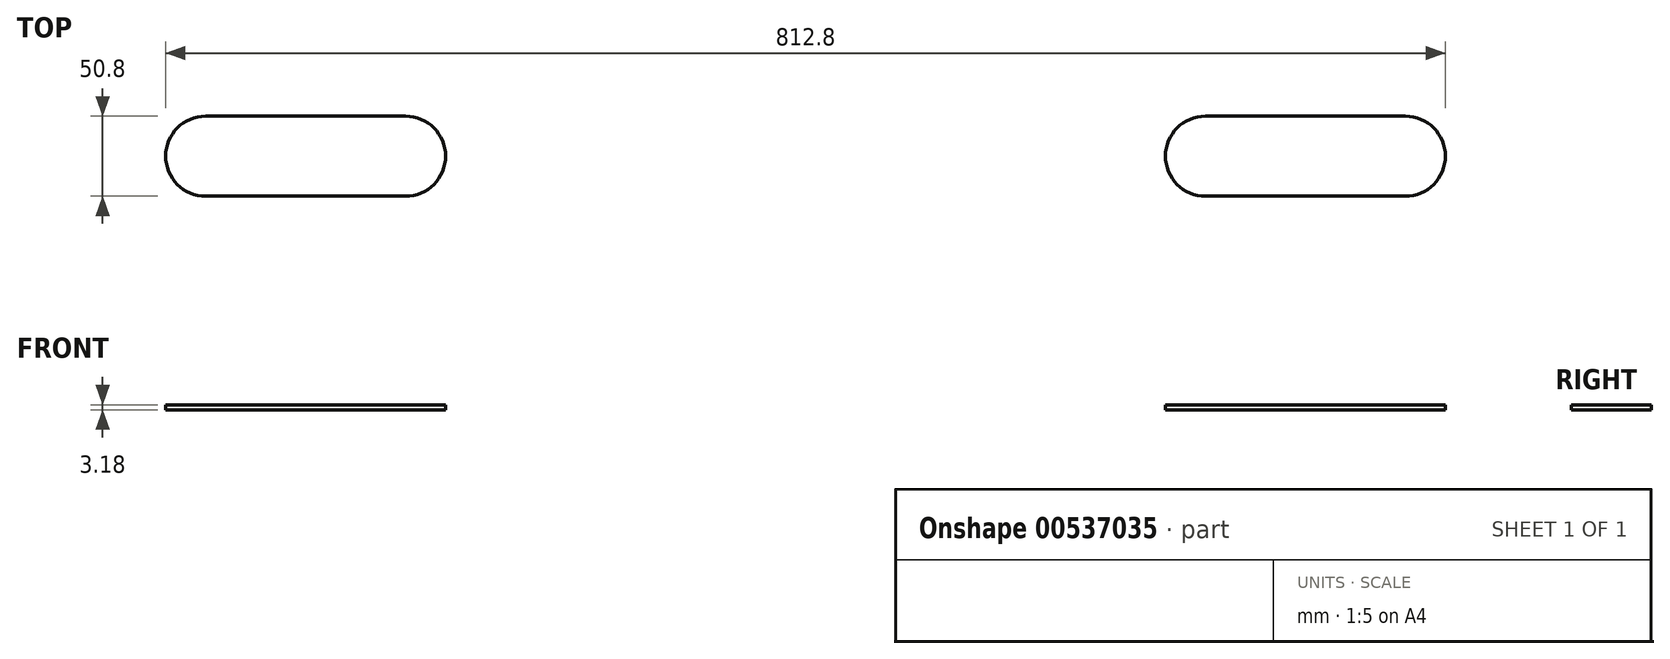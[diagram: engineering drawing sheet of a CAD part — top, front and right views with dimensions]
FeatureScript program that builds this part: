
annotation { "Feature Type Name" : "Feature", "Feature Type Description" : "" }
export const myFeature = defineFeature(function(context is Context, id is Id, definition is map)
    precondition{}
    {
        {
            var Q0;
            Q0=qCreatedBy(makeId("Right.planeOp"),FACE);
            var sketch = newSketch(context, id + "F0", { "sketchPlane" : qUnion([Q0])});
            skLineSegment(sketch, "E0.bottom", {"start": v(381, 1.59) * mm, "end": v(-381, 1.59) * mm});
            skLineSegment(sketch, "E0.top", {"start": v(381, -1.59) * mm, "end": v(-381, -1.59) * mm});
            skLineSegment(sketch, "E0.left", {"start": v(381, 1.59) * mm, "end": v(381, -1.59) * mm});
            skLineSegment(sketch, "E0.right", {"start": v(-381, 1.59) * mm, "end": v(-381, -1.59) * mm});
            skPoint(sketch, "E0.middle", {"position": v(0, 0) * mm});
            skSolve(sketch);
        }
        {
            var Q0;
            Q0=makeQuery(id+"F0.imprint","IMPRINT",FACE,{"disambiguationData":[TD([[makeQuery(id+"F0.imprint","IMPRINT",EDGE,{"derivedFrom":sQuery(id+"F0.wireOp",EDGE,"E0.bottom")}),1.0]])]});
            extrude(context, id + "F1", {"entities" : qUnion([Q0]), "endBound" : BoundingType.SYMMETRIC, "depth" : 1295.4 * mm, "offsetDistance" : 25.4 * mm});
        }
        {
            var Q0;
            Q0=makeQuery(id+"F1.opExtrude","SWEPT_FACE",FACE,{"disambiguationData":[OSD([sQuery(id+"F0.wireOp",EDGE,"E0.bottom")])]});
            var sketch = newSketch(context, id + "F2", { "sketchPlane" : qUnion([Q0])});
            skPoint(sketch, "E1", {"position": v(463.55, 228.6) * mm});
            skPoint(sketch, "E2", {"position": v(463.55, 190.5) * mm});
            skPoint(sketch, "E3.0.1.0", {"position": v(463.55, -215.9) * mm});
            skPoint(sketch, "E3.0.1.1", {"position": v(463.55, -177.8) * mm});
            skPoint(sketch, "E3.1.0.0", {"position": v(0, 190.5) * mm});
            skPoint(sketch, "E3.1.0.1", {"position": v(0, 228.6) * mm});
            skPoint(sketch, "E3.1.1.0", {"position": v(0, -215.9) * mm});
            skPoint(sketch, "E3.1.1.1", {"position": v(0, -177.8) * mm});
            skPoint(sketch, "E3.2.0.0", {"position": v(-463.55, 190.5) * mm});
            skPoint(sketch, "E3.2.0.1", {"position": v(-463.55, 228.6) * mm});
            skPoint(sketch, "E3.2.1.0", {"position": v(-463.55, -215.9) * mm});
            skPoint(sketch, "E3.2.1.1", {"position": v(-463.55, -177.8) * mm});
            skLineSegment(sketch, "E3.direction1", {"start": v(463.55, 228.6) * mm, "end": v(0, 228.6) * mm, "construction": true});
            skLineSegment(sketch, "E3.direction2", {"start": v(463.55, 228.6) * mm, "end": v(463.55, -177.8) * mm, "construction": true});
            skSolve(sketch);
        }
        {
            var Q0;
            Q0=sQuery(id+"F2.wireOp",VERTEX,"E1");
            var Q1;
            Q1=sQuery(id+"F2.wireOp",VERTEX,"E2");
            var Q2;
            Q2=sQuery(id+"F2.wireOp",VERTEX,"E3.0.1.1");
            var Q3;
            Q3=sQuery(id+"F2.wireOp",VERTEX,"E3.0.1.0");
            var Q4;
            Q4=sQuery(id+"F2.wireOp",VERTEX,"E3.1.0.1");
            var Q5;
            Q5=sQuery(id+"F2.wireOp",VERTEX,"E3.1.0.0");
            var Q6;
            Q6=sQuery(id+"F2.wireOp",VERTEX,"E3.1.1.1");
            var Q7;
            Q7=sQuery(id+"F2.wireOp",VERTEX,"E3.1.1.0");
            var Q8;
            Q8=sQuery(id+"F2.wireOp",VERTEX,"E3.2.0.0");
            var Q9;
            Q9=sQuery(id+"F2.wireOp",VERTEX,"E3.2.0.1");
            var Q10;
            Q10=sQuery(id+"F2.wireOp",VERTEX,"E3.2.1.1");
            var Q11;
            Q11=sQuery(id+"F2.wireOp",VERTEX,"E3.2.1.0");
            var Q12;
            Q12=makeQuery(id+"F1.opExtrude","SWEPT_BODY",BODY,{"disambiguationData":[OSD([sQuery(id+"F0.wireOp",EDGE,"E0.bottom"),sQuery(id+"F0.wireOp",EDGE,"E0.top"),sQuery(id+"F0.wireOp",EDGE,"E0.left"),sQuery(id+"F0.wireOp",EDGE,"E0.right")])]});
            hole(context, id + "F3", {"style" : HoleStyle.SIMPLE, "endStyle" : HoleEndStyle.THROUGH, "holeDiameter" : 11.1 * mm, "isTappedThrough" : true, "tappedDepth" : 12.7 * mm, "tapClearance" : 3, "locations" : qUnion([Q0, Q1, Q2, Q3, Q4, Q5, Q6, Q7, Q8, Q9, Q10, Q11]), "scope" : qUnion([Q12])});
        }
        {
            var Q0;
            {var subQ0=sQuery(id+"F0.wireOp",EDGE,"E0.bottom");Q0=makeQuery(id+"F2.imprint","IMPRINT",FACE,{"disambiguationData":[TD([[makeQuery(id+"F2.imprint","IMPRINT",EDGE,{"derivedFrom":makeQuery(id+"F1.opExtrude","CAP_EDGE",EDGE,{"disambiguationData":[OSD([subQ0])],"isStart":true})}),1.0]])]});}
            var sketch = newSketch(context, id + "F4", { "sketchPlane" : qUnion([Q0])});
            skLineSegment(sketch, "E4", {"start": v(254, 304.8) * mm, "end": v(381, 304.8) * mm});
            skArc(sketch, "E5.0.startCap", {"start": v(254, 279.4) * mm, "mid": v(228.6, 304.8) * mm, "end": v(254, 330.2) * mm});
            skArc(sketch, "E5.0.endCap", {"start": v(381, 330.2) * mm, "mid": v(406.4, 304.8) * mm, "end": v(381, 279.4) * mm});
            skLineSegment(sketch, "E5.0.left", {"start": v(254, 330.2) * mm, "end": v(381, 330.2) * mm});
            skLineSegment(sketch, "E5.0.right", {"start": v(254, 279.4) * mm, "end": v(381, 279.4) * mm});
            skArc(sketch, "E6.1.0.0", {"start": v(-381, 279.4) * mm, "mid": v(-406.4, 304.8) * mm, "end": v(-381, 330.2) * mm});
            skArc(sketch, "E6.1.0.1", {"start": v(-254, 330.2) * mm, "mid": v(-228.6, 304.8) * mm, "end": v(-254, 279.4) * mm});
            skLineSegment(sketch, "E6.1.0.2", {"start": v(-381, 330.2) * mm, "end": v(-254, 330.2) * mm});
            skLineSegment(sketch, "E6.1.0.3", {"start": v(-381, 279.4) * mm, "end": v(-254, 279.4) * mm});
            skLineSegment(sketch, "E6.direction1", {"start": v(254, 279.4) * mm, "end": v(-381, 279.4) * mm, "construction": true});
            skSolve(sketch);
        }
        {
            var Q0;
            Q0=makeQuery(id+"F4.imprint","IMPRINT",FACE,{"disambiguationData":[TD([[makeQuery(id+"F4.imprint","IMPRINT",EDGE,{"derivedFrom":sQuery(id+"F4.wireOp",EDGE,"E5.0.startCap")}),-1.0]])]});
            var Q1;
            Q1=makeQuery(id+"F4.imprint","IMPRINT",FACE,{"disambiguationData":[TD([[makeQuery(id+"F4.imprint","IMPRINT",EDGE,{"derivedFrom":sQuery(id+"F4.wireOp",EDGE,"E6.1.0.0")}),-1.0]])]});
            var Q2;
            Q2=makeQuery(id+"F1.opExtrude","SWEPT_FACE",FACE,{"disambiguationData":[OSD([sQuery(id+"F0.wireOp",EDGE,"E0.top")])]});
            extrude(context, id + "F5", {"entities" : qUnion([Q0, Q1]), "operationType" : NewBodyOperationType.REMOVE, "endBound" : BoundingType.UP_TO_SURFACE, "oppositeDirection" : true, "depth" : 25.4 * mm, "endBoundEntityFace" : qUnion([Q2]), "offsetDistance" : 25.4 * mm});
        }
        {
            var Q0;
            {var subQ0=sQuery(id+"F0.wireOp",EDGE,"E0.bottom");Q0=makeQuery(id+"F2.imprint","IMPRINT",FACE,{"disambiguationData":[TD([[makeQuery(id+"F2.imprint","IMPRINT",EDGE,{"derivedFrom":makeQuery(id+"F1.opExtrude","CAP_EDGE",EDGE,{"disambiguationData":[OSD([subQ0])],"isStart":true})}),1.0]])]});}
            var sketch = newSketch(context, id + "F6", { "sketchPlane" : qUnion([Q0])});
            skPoint(sketch, "E7", {"position": v(571.5, 304.8) * mm});
            skPoint(sketch, "E8.0.1.0", {"position": v(571.5, 263.53) * mm});
            skPoint(sketch, "E8.0.2.0", {"position": v(571.5, 222.25) * mm});
            skPoint(sketch, "E8.0.3.0", {"position": v(571.5, 180.98) * mm});
            skPoint(sketch, "E8.0.4.0", {"position": v(571.5, 139.7) * mm});
            skPoint(sketch, "E8.0.5.0", {"position": v(571.5, 98.43) * mm});
            skPoint(sketch, "E8.0.6.0", {"position": v(571.5, 57.15) * mm});
            skPoint(sketch, "E8.0.7.0", {"position": v(571.5, 15.88) * mm});
            skPoint(sketch, "E8.0.8.0", {"position": v(571.5, -25.4) * mm});
            skPoint(sketch, "E8.0.9.0", {"position": v(571.5, -66.67) * mm});
            skPoint(sketch, "E8.0.10.0", {"position": v(571.5, -107.95) * mm});
            skPoint(sketch, "E8.0.11.0", {"position": v(571.5, -149.22) * mm});
            skPoint(sketch, "E8.0.12.0", {"position": v(571.5, -190.5) * mm});
            skPoint(sketch, "E8.0.13.0", {"position": v(571.5, -231.77) * mm});
            skPoint(sketch, "E8.0.14.0", {"position": v(571.5, -273.05) * mm});
            skPoint(sketch, "E8.1.0.0", {"position": v(215.9, 304.8) * mm});
            skPoint(sketch, "E8.1.1.0", {"position": v(215.9, 263.53) * mm});
            skPoint(sketch, "E8.1.2.0", {"position": v(215.9, 222.25) * mm});
            skPoint(sketch, "E8.1.3.0", {"position": v(215.9, 180.98) * mm});
            skPoint(sketch, "E8.1.4.0", {"position": v(215.9, 139.7) * mm});
            skPoint(sketch, "E8.1.5.0", {"position": v(215.9, 98.43) * mm});
            skPoint(sketch, "E8.1.6.0", {"position": v(215.9, 57.15) * mm});
            skPoint(sketch, "E8.1.7.0", {"position": v(215.9, 15.88) * mm});
            skPoint(sketch, "E8.1.8.0", {"position": v(215.9, -25.4) * mm});
            skPoint(sketch, "E8.1.9.0", {"position": v(215.9, -66.67) * mm});
            skPoint(sketch, "E8.1.10.0", {"position": v(215.9, -107.95) * mm});
            skPoint(sketch, "E8.1.11.0", {"position": v(215.9, -149.22) * mm});
            skPoint(sketch, "E8.1.12.0", {"position": v(215.9, -190.5) * mm});
            skPoint(sketch, "E8.1.13.0", {"position": v(215.9, -231.77) * mm});
            skPoint(sketch, "E8.1.14.0", {"position": v(215.9, -273.05) * mm});
            skLineSegment(sketch, "E8.direction1", {"start": v(571.5, 304.8) * mm, "end": v(215.9, 304.8) * mm, "construction": true});
            skLineSegment(sketch, "E8.direction2", {"start": v(571.5, 304.8) * mm, "end": v(571.5, 263.53) * mm, "construction": true});
            skSolve(sketch);
        }
        {
            var Q0;
            Q0=sQuery(id+"F6.wireOp",VERTEX,"E7");
            var Q1;
            Q1=sQuery(id+"F6.wireOp",VERTEX,"E8.0.1.0");
            var Q2;
            Q2=sQuery(id+"F6.wireOp",VERTEX,"E8.0.2.0");
            var Q3;
            Q3=sQuery(id+"F6.wireOp",VERTEX,"E8.0.3.0");
            var Q4;
            Q4=sQuery(id+"F6.wireOp",VERTEX,"E8.0.4.0");
            var Q5;
            Q5=sQuery(id+"F6.wireOp",VERTEX,"E8.0.5.0");
            var Q6;
            Q6=sQuery(id+"F6.wireOp",VERTEX,"E8.0.7.0");
            var Q7;
            Q7=sQuery(id+"F6.wireOp",VERTEX,"E8.0.11.0");
            var Q8;
            Q8=sQuery(id+"F6.wireOp",VERTEX,"E8.0.14.0");
            var Q9;
            Q9=sQuery(id+"F6.wireOp",VERTEX,"E8.0.13.0");
            var Q10;
            Q10=sQuery(id+"F6.wireOp",VERTEX,"E8.0.12.0");
            var Q11;
            Q11=sQuery(id+"F6.wireOp",VERTEX,"E8.0.9.0");
            var Q12;
            Q12=sQuery(id+"F6.wireOp",VERTEX,"E8.0.10.0");
            var Q13;
            Q13=sQuery(id+"F6.wireOp",VERTEX,"E8.0.8.0");
            var Q14;
            Q14=sQuery(id+"F6.wireOp",VERTEX,"E8.0.6.0");
            var Q15;
            Q15=sQuery(id+"F6.wireOp",VERTEX,"E8.1.5.0");
            var Q16;
            Q16=sQuery(id+"F6.wireOp",VERTEX,"E8.1.4.0");
            var Q17;
            Q17=sQuery(id+"F6.wireOp",VERTEX,"E8.1.3.0");
            var Q18;
            Q18=sQuery(id+"F6.wireOp",VERTEX,"E8.1.2.0");
            var Q19;
            Q19=sQuery(id+"F6.wireOp",VERTEX,"E8.1.1.0");
            var Q20;
            Q20=sQuery(id+"F6.wireOp",VERTEX,"E8.1.6.0");
            var Q21;
            Q21=sQuery(id+"F6.wireOp",VERTEX,"E8.1.8.0");
            var Q22;
            Q22=sQuery(id+"F6.wireOp",VERTEX,"E8.1.7.0");
            var Q23;
            Q23=sQuery(id+"F6.wireOp",VERTEX,"E8.1.10.0");
            var Q24;
            Q24=sQuery(id+"F6.wireOp",VERTEX,"E8.1.9.0");
            var Q25;
            Q25=sQuery(id+"F6.wireOp",VERTEX,"E8.1.11.0");
            var Q26;
            Q26=sQuery(id+"F6.wireOp",VERTEX,"E8.1.12.0");
            var Q27;
            Q27=sQuery(id+"F6.wireOp",VERTEX,"E8.1.13.0");
            var Q28;
            Q28=sQuery(id+"F6.wireOp",VERTEX,"E8.1.14.0");
            var Q29;
            Q29=sQuery(id+"F6.wireOp",VERTEX,"E8.1.0.0");
            var Q30;
            Q30=makeQuery(id+"F1.opExtrude","SWEPT_BODY",BODY,{"disambiguationData":[OSD([sQuery(id+"F0.wireOp",EDGE,"E0.bottom"),sQuery(id+"F0.wireOp",EDGE,"E0.top"),sQuery(id+"F0.wireOp",EDGE,"E0.left"),sQuery(id+"F0.wireOp",EDGE,"E0.right")])]});
            hole(context, id + "F7", {"style" : HoleStyle.SIMPLE, "endStyle" : HoleEndStyle.THROUGH, "holeDiameter" : 9.52 * mm, "isTappedThrough" : true, "tappedDepth" : 12.7 * mm, "tapClearance" : 3, "locations" : qUnion([Q0, Q1, Q2, Q3, Q4, Q5, Q6, Q7, Q8, Q9, Q10, Q11, Q12, Q13, Q14, Q15, Q16, Q17, Q18, Q19, Q20, Q21, Q22, Q23, Q24, Q25, Q26, Q27, Q28, Q29]), "scope" : qUnion([Q30])});
        }
    });
